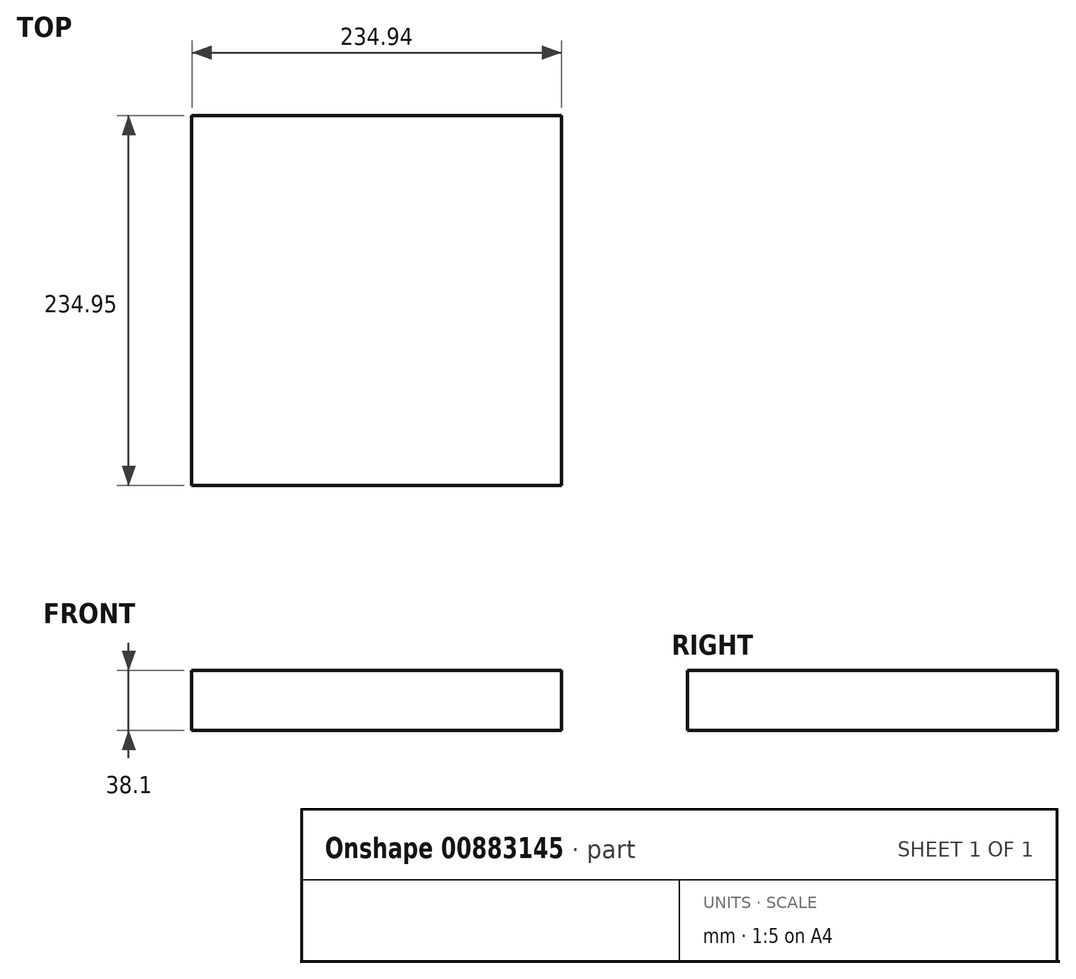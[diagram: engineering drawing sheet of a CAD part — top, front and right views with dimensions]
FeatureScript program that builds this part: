
annotation { "Feature Type Name" : "Feature", "Feature Type Description" : "" }
export const myFeature = defineFeature(function(context is Context, id is Id, definition is map)
    precondition{}
    {
        {
            var Q0;
            Q0=qCreatedBy(makeId("Front.planeOp"),FACE);
            var sketch = newSketch(context, id + "F0", { "sketchPlane" : qUnion([Q0])});
            skLineSegment(sketch, "E0.bottom", {"start": v(-117.48, 19.05) * mm, "end": v(117.47, 19.05) * mm});
            skLineSegment(sketch, "E0.top", {"start": v(-117.48, -19.05) * mm, "end": v(117.47, -19.05) * mm});
            skLineSegment(sketch, "E0.left", {"start": v(-117.48, 19.05) * mm, "end": v(-117.48, -19.05) * mm});
            skLineSegment(sketch, "E0.right", {"start": v(117.47, 19.05) * mm, "end": v(117.47, -19.05) * mm});
            skPoint(sketch, "E0.middle", {"position": v(0, 0) * mm});
            skSolve(sketch);
        }
        {
            var Q0;
            Q0=makeQuery(id+"F0.imprint","IMPRINT",FACE,{"disambiguationData":[TD([[makeQuery(id+"F0.imprint","IMPRINT",EDGE,{"derivedFrom":sQuery(id+"F0.wireOp",EDGE,"E0.bottom")}),-1.0]])]});
            extrude(context, id + "F1", {"entities" : qUnion([Q0]), "depth" : 234.95 * mm, "offsetDistance" : 25.4 * mm});
        }
    });
